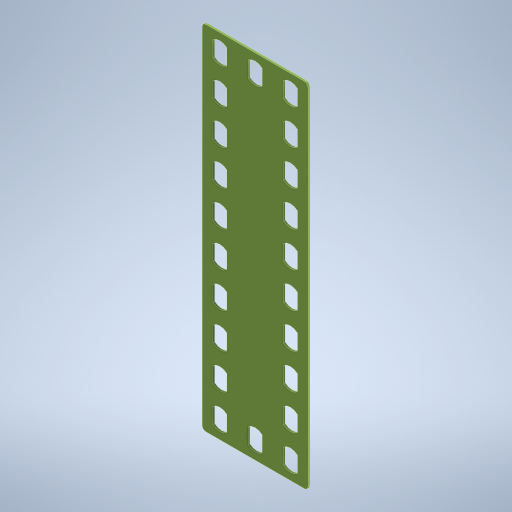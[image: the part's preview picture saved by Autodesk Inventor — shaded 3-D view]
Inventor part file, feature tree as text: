
AUTODESK INVENTOR PART (.ipt)
format: ipt  version: 2024 (Build 280153000, 153)  size: 356,864 bytes
history: native  units: mm
features: pattern_linear x4, extrude x3, fillet x3, sketch x3, other x1
ambient origin geometry x8: Origin, YZ Plane, XZ Plane, XY Plane, X Axis, Y Axis, Z Axis, Center Point
bodies: Body1 (feature_tree)
feature tree (14):
  other  "Těleso1"
  extrude  "Vysunutí1"  Depth=100.0mm
  fillet  "Zaoblení1"  Radius=30.0mm
  fillet  "Zaoblení2"  Radius=10.0mm
  fillet  "Zaoblení3"  Radius=10.0mm
  extrude  "Vysunutí3"  Depth=0.5mm TaperAngle=0.0deg
  pattern_linear  "Obdélníkové pole2"  Spacing1=1.0mm  [1 undecoded]
  pattern_linear  "Obdélníkové pole3"  Spacing1=1.0mm  [1 undecoded]
  extrude  "Vysunutí4"  Depth=1.0mm
  pattern_linear  "Obdélníkové pole4"  Spacing1=2.0mm  [1 undecoded]
  pattern_linear  "Obdélníkové pole5"  Spacing1=5.0mm  [1 undecoded]
  sketch  "Náčrt1"
  sketch  "Náčrt3"
  sketch  "Náčrt4"
note: 4 required parameter values undecoded (feature->parameter linkage not recoverable at this tier; creation-order binding heuristic only, values carry confidence <= 0.55)
